# Revit family: OEWZ
name_source: partatom
category: Mechanical Equipment
revit_build: Autodesk Revit 2017 (Build: 20181011_1645(x64)
units: mm (PartAtom-declared; Revit-internal decimal feet)

## family parameters
Always vertical = Yes
Cut with Voids When Loaded = No
OmniClass Number = 23.40.40.11.17
OmniClass Title = Refrigerated Cases
Part Type = Normal
Room Calculation Point = No
Round Connector Dimension = Use Radius
Shared = No
Work Plane-Based = Yes

## types (1)
- 04'
    BOTTOM ELECTRICAL = Yes
    BOTTOM REFRIGERATION PIPING = Yes
    CENTER LINE = 26 3/4"
    Certifications = NSF 7, UL471, CSA
    DATE = 04/18/2016
    DESIGNERS NAME = SHIDDRAMESH
    DRAIN PIPING = Yes
    Default Elevation = 48"
    Description = OEWZ - Island case
    EQUIPMENT DESCRIPTION = OEWZ - Island case
    EQUIPMENT MARK = OEWZ
    GLASS = Glass
    Height = 35"
    How Many Defrosts Per Day = 3
    Island  Case Length = 48"
    Island 208V Defrost Heaters Amps = 4 A
    Island 208V Defrost Heaters Watts = 800 A
    Island 240 Defrost Heaters Amps = 4 A
    Island 240 Defrost Heaters Watts = 1065 W
    Island Anti-Condensate Heaters Amps = 1 A
    Island Anti-Condensate Heaters Watts = 82 W
    Island BTUH Conventional = 359
    Island BTUH Parallel = 325
    Island Discharge Air Velocity (FPM) = 255 FPM
    Island Discharge Air(°F) = -10 °F
    Island Electric Fail-Safe = 50 (Min)
    Island Electric Termination Temp (F°) = 45 °F
    Island Evaporator (°F) = -22 °F
    Island Fans Per Case = 1
    Island High Efficiency Fans Amps = 0 A
    Island High Efficiency Fans Watts = 11 W
    Island Hot Gas Fail-Safe (Min) = 20 (Min)
    Island Hot Gas Termination Temp (F°) = 60 °F
    Island Run-Off Time (Min) = 5 (Min)
    Island Superheat @ Bulb Set Point (°F) = 3-5 °F
    Item Description = OEWZ - Island case
    LF STD END = Yes
    Legend Number = OEWZ
    Length = 53 1/2"
    Manufacturer = HILL PHOENIX
    Model = OEWZ
    PAINTED METAL UPPER SHELF = PAINTED SHELVES
    REAR REFRIGERATION PIPING = Yes
    REFRIGERATION PIPING = COPPER PIPE
    RT STD END = Yes
    TOP ELECTRICAL = Yes
    TOP REFRIGERATION PIPING = Yes
    URL = http://www.hillphoenix.com
    Width = 42 7/8"

## geometry (parser evidence)
native form markers: Blend x8, Sweep x3
no freeform markers — native parametric forms only
